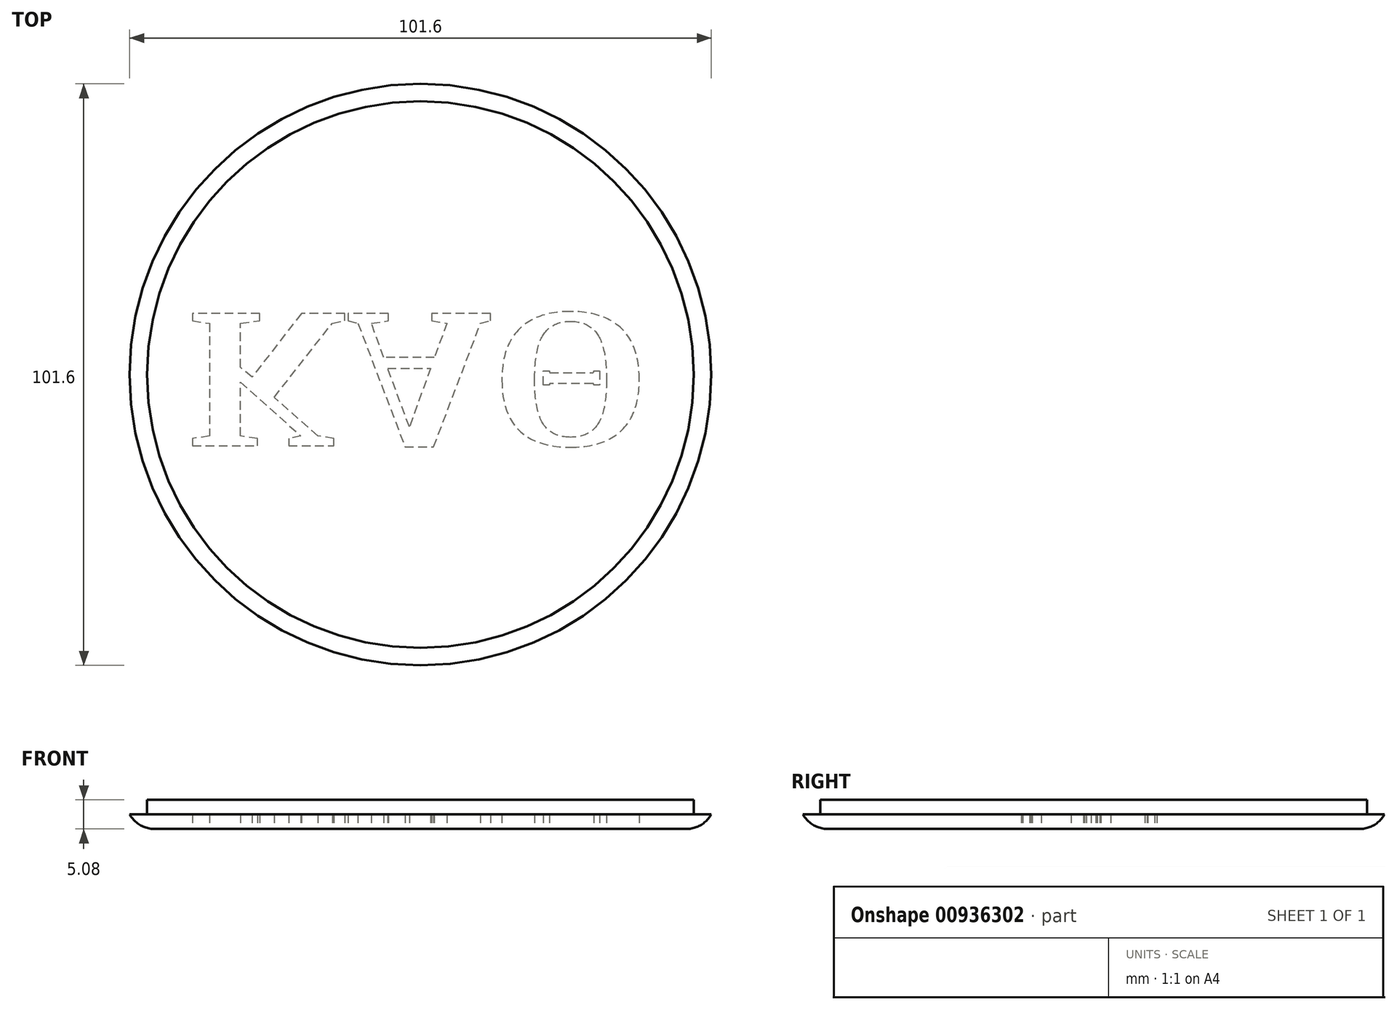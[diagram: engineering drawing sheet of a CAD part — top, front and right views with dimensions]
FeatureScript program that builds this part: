
annotation { "Feature Type Name" : "Feature", "Feature Type Description" : "" }
export const myFeature = defineFeature(function(context is Context, id is Id, definition is map)
    precondition{}
    {
        {
            var Q0;
            Q0=qCreatedBy(makeId("Top.planeOp"),FACE);
            var sketch = newSketch(context, id + "F0", { "sketchPlane" : qUnion([Q0])});
            skCircle(sketch, "E0", {"center": v(0, 0) * mm, "radius": 50.8 * mm});
            skSolve(sketch);
        }
        {
            var Q0;
            Q0 = qSketchRegion(id + "F0", true);
            extrude(context, id + "F1", {"entities" : qUnion([Q0]), "depth" : 2.54 * mm, "offsetDistance" : 25.4 * mm});
        }
        {
            var Q0;
            Q0=makeQuery(id+"F1.opExtrude","CAP_FACE",FACE,{"disambiguationData":[OSD([sQuery(id+"F0.wireOp",EDGE,"E0")])],"isStart":false});
            var sketch = newSketch(context, id + "F2", { "sketchPlane" : qUnion([Q0])});
            skCircle(sketch, "E1.0", {"center": v(0, 0) * mm, "radius": 47.75 * mm});
            skSolve(sketch);
        }
        {
            var Q0;
            Q0 = qSketchRegion(id + "F2", true);
            extrude(context, id + "F3", {"entities" : qUnion([Q0]), "operationType" : NewBodyOperationType.ADD, "depth" : 2.54 * mm, "offsetDistance" : 25.4 * mm});
        }
        {
            var Q0;
            Q0=makeQuery(id+"F1.opExtrude","CAP_EDGE",EDGE,{"disambiguationData":[OSD([sQuery(id+"F0.wireOp",EDGE,"E0")])],"isStart":true});
            fillet(context, id + "F4", {"entities" : qUnion([Q0]), "radius" : 5.08 * mm, "tangentPropagation" : true, "allowEdgeOverflow" : false});
        }
        {
            var Q0;
            Q0=makeQuery(id+"F1.opExtrude","CAP_FACE",FACE,{"disambiguationData":[OSD([sQuery(id+"F0.wireOp",EDGE,"E0")])],"isStart":true});
            var sketch = newSketch(context, id + "F5", { "sketchPlane" : qUnion([Q0])});
            skText(sketch, "E2", { "text": "KAO", "fontName": "Tinos-Bold.ttf"});
            skLineSegment(sketch, "E3", {"start": v(21.46, 1.8) * mm, "end": v(21.46, -0.65) * mm});
            skLineSegment(sketch, "E4", {"start": v(21.46, -0.65) * mm, "end": v(22.5, -0.65) * mm});
            skLineSegment(sketch, "E5", {"start": v(22.5, -0.65) * mm, "end": v(22.5, -0.5) * mm});
            skLineSegment(sketch, "E6", {"start": v(22.65, -0.36) * mm, "end": v(30.12, -0.36) * mm});
            skLineSegment(sketch, "E7", {"start": v(30.27, -0.5) * mm, "end": v(30.27, -0.65) * mm});
            skLineSegment(sketch, "E8", {"start": v(30.27, -0.65) * mm, "end": v(31.31, -0.65) * mm});
            skLineSegment(sketch, "E9", {"start": v(31.31, -0.65) * mm, "end": v(31.31, 1.8) * mm});
            skLineSegment(sketch, "E10", {"start": v(31.31, 1.8) * mm, "end": v(30.27, 1.8) * mm});
            skLineSegment(sketch, "E11", {"start": v(30.27, 1.8) * mm, "end": v(30.27, 1.72) * mm});
            skLineSegment(sketch, "E12", {"start": v(30.12, 1.57) * mm, "end": v(22.65, 1.57) * mm});
            skLineSegment(sketch, "E13", {"start": v(22.5, 1.72) * mm, "end": v(22.5, 1.8) * mm});
            skLineSegment(sketch, "E14", {"start": v(22.5, 1.8) * mm, "end": v(21.46, 1.8) * mm});
            skPoint(sketch, "E15.visualSharp", {"position": v(22.5, 1.57) * mm});
            skArc(sketch, "E15.filletArc", {"start": v(22.5, 1.72) * mm, "mid": v(22.54, 1.62) * mm, "end": v(22.65, 1.57) * mm});
            skPoint(sketch, "E16.visualSharp", {"position": v(22.5, -0.36) * mm});
            skArc(sketch, "E16.filletArc", {"start": v(22.65, -0.36) * mm, "mid": v(22.54, -0.4) * mm, "end": v(22.5, -0.5) * mm});
            skPoint(sketch, "E17.visualSharp", {"position": v(30.27, 1.57) * mm});
            skArc(sketch, "E17.filletArc", {"start": v(30.12, 1.57) * mm, "mid": v(30.22, 1.62) * mm, "end": v(30.27, 1.72) * mm});
            skPoint(sketch, "E18.visualSharp", {"position": v(30.27, -0.36) * mm});
            skArc(sketch, "E18.filletArc", {"start": v(30.27, -0.5) * mm, "mid": v(30.22, -0.4) * mm, "end": v(30.12, -0.36) * mm});
            const initialGuessF5  = {"E2": [-0.04042, -0.01068, 1, 0, 0.0254]};
            skSetInitialGuess(sketch, initialGuessF5);
            skSolve(sketch);
        }
        {
            var Q0;
            Q0 = qSketchRegion(id + "F5", true);
            var Q1;
            Q1=makeQuery(id+"F5.imprint","IMPRINT",FACE,{"disambiguationData":[TD([[makeQuery(id+"F5.imprint","IMPRINT",EDGE,{"derivedFrom":sQuery(id+"F5.wireOp",EDGE,"E3")}),1.0]])]});
            extrude(context, id + "F6", {"entities" : qUnion([Q0, Q1]), "operationType" : NewBodyOperationType.REMOVE, "oppositeDirection" : true, "depth" : 2.54 * mm, "offsetDistance" : 25.4 * mm});
        }
    });
